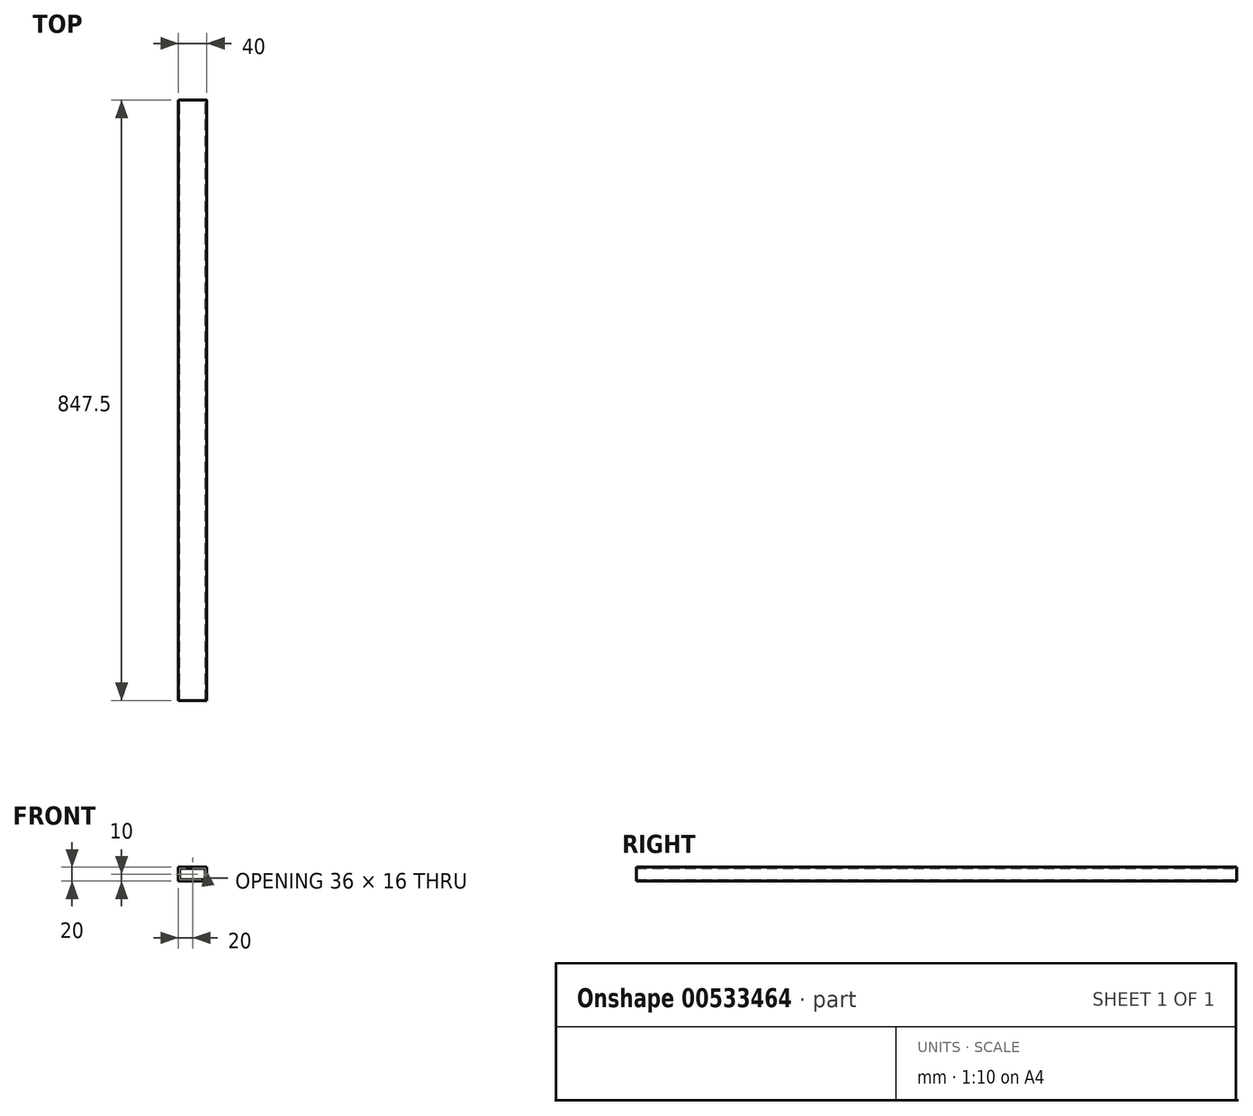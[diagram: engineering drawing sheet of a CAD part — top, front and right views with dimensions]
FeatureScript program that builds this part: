
annotation { "Feature Type Name" : "Feature", "Feature Type Description" : "" }
export const myFeature = defineFeature(function(context is Context, id is Id, definition is map)
    precondition{}
    {
        {
            var Q0;
            Q0=qCreatedBy(makeId("Front.planeOp"),FACE);
            var sketch = newSketch(context, id + "F0", { "sketchPlane" : qUnion([Q0])});
            skLineSegment(sketch, "E0.bottom", {"start": v(1, 0) * mm, "end": v(39, 0) * mm});
            skLineSegment(sketch, "E0.top", {"start": v(1, 20) * mm, "end": v(39, 20) * mm});
            skLineSegment(sketch, "E0.left", {"start": v(0, 1) * mm, "end": v(0, 19) * mm});
            skLineSegment(sketch, "E0.right", {"start": v(40, 1) * mm, "end": v(40, 19) * mm});
            skLineSegment(sketch, "E1.bottom", {"start": v(3, 2) * mm, "end": v(37, 2) * mm});
            skLineSegment(sketch, "E1.top", {"start": v(3, 18) * mm, "end": v(37, 18) * mm});
            skLineSegment(sketch, "E1.left", {"start": v(2, 3) * mm, "end": v(2, 17) * mm});
            skLineSegment(sketch, "E1.right", {"start": v(38, 3) * mm, "end": v(38, 17) * mm});
            skPoint(sketch, "E2.visualSharp", {"position": v(2, 18) * mm});
            skArc(sketch, "E2.filletArc", {"start": v(3, 18) * mm, "mid": v(2.3, 17.7) * mm, "end": v(2, 17) * mm});
            skPoint(sketch, "E3.visualSharp", {"position": v(38, 18) * mm});
            skArc(sketch, "E3.filletArc", {"start": v(38, 17) * mm, "mid": v(37.7, 17.7) * mm, "end": v(37, 18) * mm});
            skPoint(sketch, "E4.visualSharp", {"position": v(38, 2) * mm});
            skArc(sketch, "E4.filletArc", {"start": v(37, 2) * mm, "mid": v(37.7, 2.3) * mm, "end": v(38, 3) * mm});
            skPoint(sketch, "E5.visualSharp", {"position": v(2, 2) * mm});
            skArc(sketch, "E5.filletArc", {"start": v(2, 3) * mm, "mid": v(2.3, 2.3) * mm, "end": v(3, 2) * mm});
            skPoint(sketch, "E6.visualSharp", {"position": v(0, 20) * mm});
            skArc(sketch, "E6.filletArc", {"start": v(1, 20) * mm, "mid": v(0.3, 19.7) * mm, "end": v(0, 19) * mm});
            skPoint(sketch, "E7.visualSharp", {"position": v(40, 20) * mm});
            skArc(sketch, "E7.filletArc", {"start": v(40, 19) * mm, "mid": v(39.7, 19.7) * mm, "end": v(39, 20) * mm});
            skPoint(sketch, "E8.visualSharp", {"position": v(40, 0) * mm});
            skArc(sketch, "E8.filletArc", {"start": v(39, 0) * mm, "mid": v(39.7, 0.3) * mm, "end": v(40, 1) * mm});
            skPoint(sketch, "E9.visualSharp", {"position": v(0, 0) * mm});
            skArc(sketch, "E9.filletArc", {"start": v(0, 1) * mm, "mid": v(0.3, 0.3) * mm, "end": v(1, 0) * mm});
            skSolve(sketch);
        }
        {
            var Q0;
            Q0=makeQuery(id+"F0.imprint","IMPRINT",FACE,{"disambiguationData":[TD([[makeQuery(id+"F0.imprint","IMPRINT",EDGE,{"derivedFrom":sQuery(id+"F0.wireOp",EDGE,"E0.bottom")}),1.0]])]});
            extrude(context, id + "F1", {"entities" : qUnion([Q0]), "depth" : 847.5 * mm, "offsetDistance" : 25 * mm});
        }
    });
